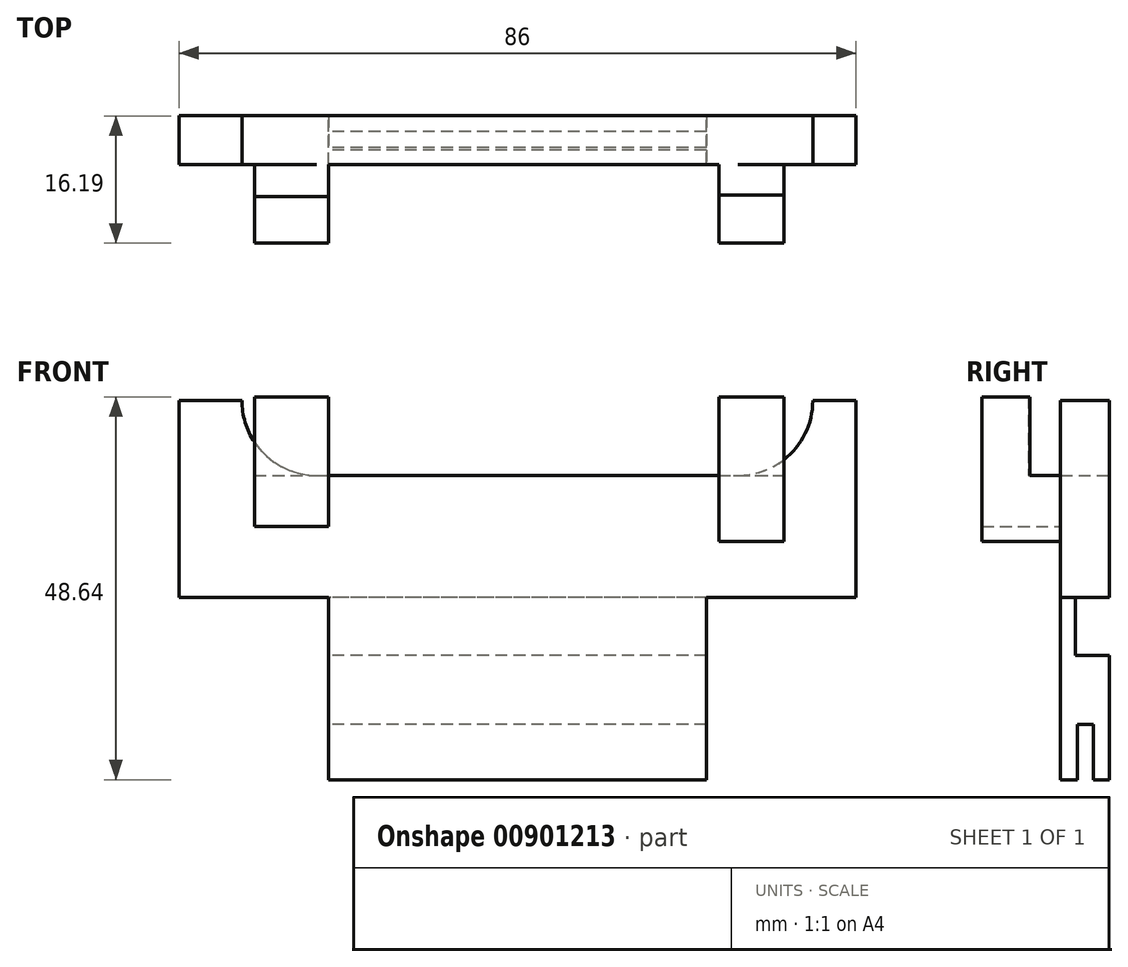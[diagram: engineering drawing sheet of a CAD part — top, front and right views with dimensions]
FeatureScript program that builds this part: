
annotation { "Feature Type Name" : "Feature", "Feature Type Description" : "" }
export const myFeature = defineFeature(function(context is Context, id is Id, definition is map)
    precondition{}
    {
        {
            var Q0;
            Q0=qCreatedBy(makeId("Right.planeOp"),FACE);
            var sketch = newSketch(context, id + "F0", { "sketchPlane" : qUnion([Q0])});
            skLineSegment(sketch, "E0", {"start": v(-2.26, 4.48) * mm, "end": v(-2.26, 11.48) * mm});
            skLineSegment(sketch, "E1", {"start": v(-2.26, 11.48) * mm, "end": v(-0.26, 11.48) * mm});
            skLineSegment(sketch, "E2", {"start": v(-0.26, 11.48) * mm, "end": v(-0.26, 4.48) * mm});
            skLineSegment(sketch, "E3", {"start": v(-0.26, 4.48) * mm, "end": v(1.77, 4.48) * mm});
            skLineSegment(sketch, "E4", {"start": v(1.77, 4.48) * mm, "end": v(1.77, 20.23) * mm});
            skLineSegment(sketch, "E5", {"start": v(1.77, 20.23) * mm, "end": v(-2.57, 20.23) * mm});
            skLineSegment(sketch, "E6", {"start": v(-2.57, 20.23) * mm, "end": v(-2.57, 27.62) * mm});
            skLineSegment(sketch, "E7", {"start": v(-2.57, 27.62) * mm, "end": v(1.77, 27.62) * mm});
            skLineSegment(sketch, "E8", {"start": v(1.77, 27.62) * mm, "end": v(1.77, 52.62) * mm});
            skLineSegment(sketch, "E9", {"start": v(1.77, 52.62) * mm, "end": v(-4.42, 52.62) * mm});
            skLineSegment(sketch, "E10", {"start": v(-4.42, 52.62) * mm, "end": v(-4.42, 4.48) * mm});
            skLineSegment(sketch, "E11", {"start": v(-4.42, 4.48) * mm, "end": v(-2.26, 4.48) * mm});
            skSolve(sketch);
        }
        {
            var Q0;
            Q0=makeQuery(id+"F0.imprint","IMPRINT",FACE,{"disambiguationData":[TD([[makeQuery(id+"F0.imprint","IMPRINT",EDGE,{"derivedFrom":sQuery(id+"F0.wireOp",EDGE,"E0")}),1.0]])]});
            extrude(context, id + "F1", {"entities" : qUnion([Q0]), "depth" : 48 * mm, "offsetDistance" : 25 * mm});
        }
        {
            var Q0;
            Q0=makeQuery(id+"F1.opExtrude","CAP_FACE",FACE,{"disambiguationData":[OSD([sQuery(id+"F0.wireOp",EDGE,"E0"),sQuery(id+"F0.wireOp",EDGE,"E1"),sQuery(id+"F0.wireOp",EDGE,"E2"),sQuery(id+"F0.wireOp",EDGE,"E3"),sQuery(id+"F0.wireOp",EDGE,"E4"),sQuery(id+"F0.wireOp",EDGE,"E5"),sQuery(id+"F0.wireOp",EDGE,"E6"),sQuery(id+"F0.wireOp",EDGE,"E7"),sQuery(id+"F0.wireOp",EDGE,"E8"),sQuery(id+"F0.wireOp",EDGE,"E9"),sQuery(id+"F0.wireOp",EDGE,"E10"),sQuery(id+"F0.wireOp",EDGE,"E11")])],"isStart":true});
            var sketch = newSketch(context, id + "F2", { "sketchPlane" : qUnion([Q0])});
            skLineSegment(sketch, "E12", {"start": v(4.42, 27.62) * mm, "end": v(-1.77, 27.62) * mm});
            skLineSegment(sketch, "E13", {"start": v(-1.77, 27.62) * mm, "end": v(-1.77, 52.62) * mm});
            skLineSegment(sketch, "E14", {"start": v(-1.77, 52.62) * mm, "end": v(4.42, 52.62) * mm});
            skLineSegment(sketch, "E15", {"start": v(4.42, 52.62) * mm, "end": v(4.42, 27.62) * mm});
            skSolve(sketch);
        }
        {
            var Q0;
            {var subQ0=sQuery(id+"F2.wireOp",EDGE,"E13");Q0=makeQuery(id+"F2.imprint","IMPRINT",FACE,{"disambiguationData":[TD([[makeQuery(id+"F2.imprint","IMPRINT",EDGE,{"derivedFrom":subQ0}),-1.0]])]});}
            extrude(context, id + "F3", {"entities" : qUnion([Q0]), "operationType" : NewBodyOperationType.ADD, "depth" : 19 * mm, "offsetDistance" : 25 * mm});
        }
        {
            var Q0;
            Q0=makeQuery(id+"F1.opExtrude","CAP_FACE",FACE,{"disambiguationData":[OSD([sQuery(id+"F0.wireOp",EDGE,"E0"),sQuery(id+"F0.wireOp",EDGE,"E1"),sQuery(id+"F0.wireOp",EDGE,"E2"),sQuery(id+"F0.wireOp",EDGE,"E3"),sQuery(id+"F0.wireOp",EDGE,"E4"),sQuery(id+"F0.wireOp",EDGE,"E5"),sQuery(id+"F0.wireOp",EDGE,"E6"),sQuery(id+"F0.wireOp",EDGE,"E7"),sQuery(id+"F0.wireOp",EDGE,"E8"),sQuery(id+"F0.wireOp",EDGE,"E9"),sQuery(id+"F0.wireOp",EDGE,"E10"),sQuery(id+"F0.wireOp",EDGE,"E11")])],"isStart":false});
            var sketch = newSketch(context, id + "F4", { "sketchPlane" : qUnion([Q0])});
            skLineSegment(sketch, "E16", {"start": v(-4.42, 52.62) * mm, "end": v(1.77, 52.62) * mm});
            skLineSegment(sketch, "E17", {"start": v(1.77, 52.62) * mm, "end": v(1.77, 27.62) * mm});
            skLineSegment(sketch, "E18", {"start": v(1.77, 27.62) * mm, "end": v(-4.42, 27.62) * mm});
            skLineSegment(sketch, "E19", {"start": v(-4.42, 27.62) * mm, "end": v(-4.42, 52.62) * mm});
            skSolve(sketch);
        }
        {
            var Q0;
            Q0=makeQuery(id+"F4.imprint","IMPRINT",FACE,{"disambiguationData":[TD([[makeQuery(id+"F4.imprint","IMPRINT",EDGE,{"derivedFrom":sQuery(id+"F4.wireOp",EDGE,"E16")}),1.0]])]});
            extrude(context, id + "F5", {"entities" : qUnion([Q0]), "operationType" : NewBodyOperationType.ADD, "depth" : 19 * mm, "offsetDistance" : 25 * mm});
        }
        {
            var Q0;
            Q0=makeQuery(id+"F5.boolean.opBoolean","MERGE",FACE,{"derivedFrom":[makeQuery(id+"F3.boolean.opBoolean","MERGE",FACE,{"derivedFrom":[makeQuery(id+"F1.opExtrude","SWEPT_FACE",FACE,{"disambiguationData":[OSD([sQuery(id+"F0.wireOp",EDGE,"E8")])]}),makeQuery(id+"F3.opExtrude","SWEPT_FACE",FACE,{"disambiguationData":[OSD([sQuery(id+"F2.wireOp",EDGE,"E13")])]})]}),makeQuery(id+"F5.opExtrude","SWEPT_FACE",FACE,{"disambiguationData":[OSD([sQuery(id+"F4.wireOp",EDGE,"E17")])]})]});
            var sketch = newSketch(context, id + "F6", { "sketchPlane" : qUnion([Q0])});
            skCircle(sketch, "E20", {"center": v(-52.02, 52.62) * mm, "radius": 9.5 * mm});
            skCircle(sketch, "E21", {"center": v(1.48, 52.62) * mm, "radius": 9.5 * mm});
            skLineSegment(sketch, "E22", {"start": v(1.48, 43.12) * mm, "end": v(-52.02, 43.12) * mm});
            skLineSegment(sketch, "E23", {"start": v(-42.52, 52.62) * mm, "end": v(-8.02, 52.62) * mm});
            skSolve(sketch);
        }
        {
            var Q0;
            {var subQ0=sQuery(id+"F6.wireOp",EDGE,"E20");var subQ1=makeQuery(id+"F5.boolean.opBoolean","MERGE",EDGE,{"derivedFrom":[makeQuery(id+"F3.boolean.opBoolean","MERGE",EDGE,{"derivedFrom":[makeQuery(id+"F1.opExtrude","SWEPT_EDGE",EDGE,{"disambiguationData":[OSD([sQuery(id+"F0.wireOp",EDGE,"E8"),sQuery(id+"F0.wireOp",EDGE,"E9")])]}),makeQuery(id+"F3.opExtrude","SWEPT_EDGE",EDGE,{"disambiguationData":[OSD([sQuery(id+"F2.wireOp",EDGE,"E13"),sQuery(id+"F2.wireOp",EDGE,"E14")])]})]}),makeQuery(id+"F5.opExtrude","SWEPT_EDGE",EDGE,{"disambiguationData":[OSD([sQuery(id+"F4.wireOp",EDGE,"E16"),sQuery(id+"F4.wireOp",EDGE,"E17")])]})]});var subQ2=makeQuery(id+"F6.imprint","INTERSECT",VERTEX,{"disambiguationData":[OD(0.0)],"derivedFrom":[subQ1,subQ0]});Q0=makeQuery(id+"F6.imprint","IMPRINT",FACE,{"disambiguationData":[TD([[makeQuery(id+"F6.imprint","IMPRINT",EDGE,{"disambiguationData":[TD([[subQ2,-1.0]])],"derivedFrom":subQ0}),1.0]])]});}
            var Q1;
            {var subQ0=sQuery(id+"F6.wireOp",EDGE,"E21");var subQ1=makeQuery(id+"F5.boolean.opBoolean","MERGE",EDGE,{"derivedFrom":[makeQuery(id+"F3.boolean.opBoolean","MERGE",EDGE,{"derivedFrom":[makeQuery(id+"F1.opExtrude","SWEPT_EDGE",EDGE,{"disambiguationData":[OSD([sQuery(id+"F0.wireOp",EDGE,"E8"),sQuery(id+"F0.wireOp",EDGE,"E9")])]}),makeQuery(id+"F3.opExtrude","SWEPT_EDGE",EDGE,{"disambiguationData":[OSD([sQuery(id+"F2.wireOp",EDGE,"E13"),sQuery(id+"F2.wireOp",EDGE,"E14")])]})]}),makeQuery(id+"F5.opExtrude","SWEPT_EDGE",EDGE,{"disambiguationData":[OSD([sQuery(id+"F4.wireOp",EDGE,"E16"),sQuery(id+"F4.wireOp",EDGE,"E17")])]})]});var subQ2=makeQuery(id+"F6.imprint","INTERSECT",VERTEX,{"disambiguationData":[OD(0.0)],"derivedFrom":[subQ1,subQ0]});Q1=makeQuery(id+"F6.imprint","IMPRINT",FACE,{"disambiguationData":[TD([[makeQuery(id+"F6.imprint","IMPRINT",EDGE,{"disambiguationData":[TD([[subQ2,1.0]])],"derivedFrom":subQ0}),1.0]])]});}
            var Q2;
            {var subQ0=sQuery(id+"F6.wireOp",EDGE,"E22");Q2=makeQuery(id+"F6.imprint","IMPRINT",FACE,{"disambiguationData":[TD([[makeQuery(id+"F6.imprint","IMPRINT",EDGE,{"derivedFrom":subQ0}),-1.0]])]});}
            extrude(context, id + "F7", {"entities" : qUnion([Q0, Q1, Q2]), "operationType" : NewBodyOperationType.REMOVE, "oppositeDirection" : true, "depth" : 25 * mm, "offsetDistance" : 25 * mm});
        }
        {
            var Q0;
            Q0=makeQuery(id+"F5.boolean.opBoolean","MERGE",FACE,{"derivedFrom":[makeQuery(id+"F3.boolean.opBoolean","MERGE",FACE,{"derivedFrom":[makeQuery(id+"F1.opExtrude","SWEPT_FACE",FACE,{"disambiguationData":[OSD([sQuery(id+"F0.wireOp",EDGE,"E10")])]}),makeQuery(id+"F3.opExtrude","SWEPT_FACE",FACE,{"disambiguationData":[OSD([sQuery(id+"F2.wireOp",EDGE,"E15")])]})]}),makeQuery(id+"F5.opExtrude","SWEPT_FACE",FACE,{"disambiguationData":[OSD([sQuery(id+"F4.wireOp",EDGE,"E19")])]})]});
            var sketch = newSketch(context, id + "F8", { "sketchPlane" : qUnion([Q0])});
            skLineSegment(sketch, "E24.bottom", {"start": v(49.58, 43.12) * mm, "end": v(57.84, 43.12) * mm});
            skLineSegment(sketch, "E24.top", {"start": v(49.58, 34.75) * mm, "end": v(57.84, 34.75) * mm});
            skLineSegment(sketch, "E24.left", {"start": v(49.58, 43.12) * mm, "end": v(49.58, 34.75) * mm});
            skLineSegment(sketch, "E24.right", {"start": v(57.84, 43.12) * mm, "end": v(57.84, 34.75) * mm});
            skLineSegment(sketch, "E25.bottom", {"start": v(-9.4, 43.12) * mm, "end": v(0, 43.12) * mm});
            skLineSegment(sketch, "E25.top", {"start": v(-9.4, 36.64) * mm, "end": v(0, 36.64) * mm});
            skLineSegment(sketch, "E25.left", {"start": v(-9.4, 43.12) * mm, "end": v(-9.4, 36.64) * mm});
            skLineSegment(sketch, "E25.right", {"start": v(0, 43.12) * mm, "end": v(0, 36.64) * mm});
            skSolve(sketch);
        }
        {
            var Q0;
            Q0=makeQuery(id+"F8.imprint","IMPRINT",FACE,{"disambiguationData":[TD([[makeQuery(id+"F8.imprint","IMPRINT",EDGE,{"derivedFrom":sQuery(id+"F8.wireOp",EDGE,"E25.bottom")}),-1.0]])]});
            var Q1;
            Q1=makeQuery(id+"F8.imprint","IMPRINT",FACE,{"disambiguationData":[TD([[makeQuery(id+"F8.imprint","IMPRINT",EDGE,{"derivedFrom":sQuery(id+"F8.wireOp",EDGE,"E24.bottom")}),-1.0]])]});
            extrude(context, id + "F9", {"entities" : qUnion([Q0, Q1]), "operationType" : NewBodyOperationType.ADD, "depth" : 10 * mm, "offsetDistance" : 25 * mm});
        }
        {
            var Q0;
            Q0=makeQuery(id+"F9.opExtrude","SWEPT_FACE",FACE,{"disambiguationData":[OSD([sQuery(id+"F8.wireOp",EDGE,"E25.bottom")])]});
            var sketch = newSketch(context, id + "F10", { "sketchPlane" : qUnion([Q0])});
            skLineSegment(sketch, "E26", {"start": v(-9.4, -8.48) * mm, "end": v(0, -8.48) * mm});
            skLineSegment(sketch, "E27", {"start": v(0, -8.48) * mm, "end": v(0, -14.42) * mm});
            skLineSegment(sketch, "E28", {"start": v(0, -14.42) * mm, "end": v(-9.4, -14.42) * mm});
            skLineSegment(sketch, "E29", {"start": v(-9.4, -14.42) * mm, "end": v(-9.4, -8.48) * mm});
            skSolve(sketch);
        }
        {
            var Q0;
            Q0=makeQuery(id+"F10.imprint","IMPRINT",FACE,{"disambiguationData":[TD([[makeQuery(id+"F10.imprint","IMPRINT",EDGE,{"derivedFrom":sQuery(id+"F10.wireOp",EDGE,"E26")}),-1.0]])]});
            extrude(context, id + "F11", {"entities" : qUnion([Q0]), "operationType" : NewBodyOperationType.ADD, "depth" : 10 * mm, "offsetDistance" : 25 * mm});
        }
        {
            var Q0;
            Q0=makeQuery(id+"F9.opExtrude","SWEPT_FACE",FACE,{"disambiguationData":[OSD([sQuery(id+"F8.wireOp",EDGE,"E24.bottom")])]});
            var sketch = newSketch(context, id + "F12", { "sketchPlane" : qUnion([Q0])});
            skLineSegment(sketch, "E30", {"start": v(49.58, -8.32) * mm, "end": v(57.84, -8.32) * mm});
            skLineSegment(sketch, "E31", {"start": v(57.84, -8.32) * mm, "end": v(57.84, -14.42) * mm});
            skLineSegment(sketch, "E32", {"start": v(57.84, -14.42) * mm, "end": v(49.58, -14.42) * mm});
            skLineSegment(sketch, "E33", {"start": v(49.58, -14.42) * mm, "end": v(49.58, -8.32) * mm});
            skSolve(sketch);
        }
        {
            var Q0;
            Q0=makeQuery(id+"F12.imprint","IMPRINT",FACE,{"disambiguationData":[TD([[makeQuery(id+"F12.imprint","IMPRINT",EDGE,{"derivedFrom":sQuery(id+"F12.wireOp",EDGE,"E30")}),-1.0]])]});
            extrude(context, id + "F13", {"entities" : qUnion([Q0]), "operationType" : NewBodyOperationType.ADD, "depth" : 10 * mm, "offsetDistance" : 25 * mm});
        }
    });
